# Revit family: KingswayGroup_TltRllHldrs_Anti-LigatureToiletRollHolderRecessed
name_source: partatom
category: Specialty Equipment
units: mm (PartAtom-declared; Revit-internal decimal feet)

## family parameters
Always vertical = Yes
Cut with Voids When Loaded = No
Part Type = Normal
Room Calculation Point = No
Round Connector Dimension = Use Diameter
Shared = No
Work Plane-Based = No

## types (1)
- KingswayGroup_TltRllHldrs_Anti-LigatureToiletRollHolderRecessed
    AssetType = Fixed
    BIMObjectName = KingswayGroup_ToiletRollHolders_Anti-LigatureToiletRollHolderRecessed
    Category = Pr_40_20_76_88:Toilet roll holders
    Color = For full range of available finishes and colours, contact Kingsway Group
    Default Elevation = 0 mm  [stored 0 ft]
    Description = Recessed Toilet Roll Holder
    DurationUnit = year
    Features = The recessed Anti-Ligature Toilet Roll Holder provides a secure and effective means of safely dispensing standard toilet rolls in patient accessible toilet facilities. Manufactured from 316 grade stainless steel for maximum corrosion resistance, the KG13 Anti-Ligature Toilet Roll Holder offers a highly durable solution. To further reduce risk, the unit is secured with anti-tamper fixings.
    Finish = For full range of available finishes and colours, contact Kingsway Group
    Grade = 316
    HolderMaterial = NBS_Concept
    IfcExportAs = IfcFurnitureType
    IfcExportType = USERDEFINED
    Manufacturer = Kingsway Group
    ManufacturerName = Kingsway Group
    ManufacturerURL = https://kingswaygroupglobal.com
    Material = Stainless Steel
    Model = KG13
    ModelNumber = KG13
    ModelReference = Anti-Ligature Toilet Roll Holder (Recessed)
    Name = ToiletRollHolders_Anti-LigatureToiletRollHolderRecessed_KG13_KingswayGroup
    NominalHeight = 203 mm  [stored 0.66601 ft]
    NominalLength = 178 mm  [stored 0.58399 ft]
    NominalWidth = 99 mm  [stored 0.324803 ft]
    ProductInformation = https://kingswaygroupglobal.com
    Size = 178 x 203 x 99 mm
    URL = https://kingswaygroupglobal.com
    Uniclass2015Code = Pr_40_20_76_88
    Uniclass2015Title = Toilet roll holders
    Uniclass2015Version = Products v1.36
    Version = 1
    WarrantyDescription = 5-Year Guarantee *For faulty manufacture and not for damage
    WarrantyDurationParts = 5
    WarrantyDurationUnit = year

note: [stored X ft] marks values corroborated as IEEE doubles in the binary element streams (Revit-internal decimal feet)

## geometry (parser evidence)
native form markers: Sweep x2
no freeform markers — native parametric forms only
